# Revit family: UNB_Specchio_Multiproduct_BIM_IT_T3588;T3589;T3590;T3591;T3592;T3593_NEW
name_source: partatom
category: Plumbing Fixtures
revit_build: Autodesk Revit 2017 (Build: 20160225_1515(x64)
units: mm (PartAtom-declared; Revit-internal decimal feet)

## family parameters
Cut with Voids When Loaded = No
Host = Face
Part Type = Normal
Room Calculation Point = No
Round Connector Dimension = Use Diameter
Shared = No

## types (6) — shared parameters
Accessori = http://www.idealstandard.it
AltezzaNominale = 700 mm  [stored 2.29659 ft]
Autore = Ideal Standard
Brand = Ideal Standard
CodiceDiPrestazione = EN
Colore = specchio
Connessione = piombatura
Default Elevation = 1500 mm
DescrizioneClassifcazioneUni2015 = Bathroom furniture
Finitura = specchio
Forma = rettangolare
Garanzia = garanzia del produttore
IfcEsportaCome = BATHROOM FURNITURE
InformazioniDiProdotto = http://www.idealstandard.it
InstruzioniInstallazione = http://www.idealstandard.it
LunghezzaNominale = 170 mm
Materiale = bicchiere
PartiDiRicambio = http://www.idealstandard.it
ProfonditàNominale = 170 mm
Revisione = 1
RiferimentoClassificazioneUni2015 = MIRRORS
Spazio = interno
Telefono = 800 652 290
TipoDiDato = Fisso
TipoEspotazioneIfc = IfcFurnitureType
TipologiaVaso = Altro
URL = http://www.idealstandard.it
UnitàDurata = anno
UnitàDurataGaranzia = anno
UnitàLineare = millimetro
UnitàMonetaria = €
UnitàSuperficie = millimetro
UnitàVolume = litro
Versione = 1
VersioneClassificazioneUni2015 = IfcFurnitureType
zero-valued in all types: Cost, CostoDiSostituzione

## per-type parameters (varying)
| type | Caratteristiche | CodiceABarre | Description | DoubleUnitsOnly | LarghezzaNominale | Model | ModelloDiRiferimento | Nome | NomeOggettoBim | NumeroDiModello | PesoNetto | Riferimento | SingleUnitsOnly |
| T3588 - 500 x 700 mirror cabinets | SPECCHIO CONT. LOW 50X70 MATT AL | 8014140447870 | SPECCHIO CONT. LOW 50X70 MATT AL | No | 500 mm | T3588AL | SPECCHIO CONT. LOW 50X70 MATT AL | ISI_IdealStandard_Specchio_T3588 | ISI_IdealStandard_Specchio_T3588 | T3588AL | 14.50 Kg | T3588 | Yes |
| T3589 - 600 x 700 mirror cabinets | SPECCHIO CONT. LOW 60X70 MATT AL | 8014140447894 | SPECCHIO CONT. LOW 60X70 MATT AL | No | 600 mm | T3589AL | SPECCHIO CONT. LOW 60X70 MATT AL | ISI_IdealStandard_Specchio_T3589 | ISI_IdealStandard_Specchio_T3589 | T3589AL | 16.00 Kg | T3589 | Yes |
| T3590 - 700 x 700 mirror cabinets | SPECCHIO CONT. LOW 70X70 MATT AL | 8014140447917 | SPECCHIO CONT. LOW 70X70 MATT AL | Yes | 700 mm  [stored 2.29659 ft] | T3590AL | SPECCHIO CONT. LOW 70X70 MATT AL | ISI_IdealStandard_Specchio_T3590 | ISI_IdealStandard_Specchio_T3590 | T3590AL | 18.00 Kg | T3590 | No |
| T3591 - 800 x 700 mirror cabinets | SPECCHIO CONT. LOW 80X70 MATT AL | 8014140447931 | SPECCHIO CONT. LOW 80X70 MATT AL | Yes | 800 mm | T3591AL | SPECCHIO CONT. LOW 80X70 MATT AL | ISI_IdealStandard_Specchio_T3591 | ISI_IdealStandard_Specchio_T3591 | T3591AL | 20.00 Kg | T3591 | No |
| T3592 - 1000 x 700 mirror cabinets | SPECCHIO CONT. LOW 100X70 MATT AL | 8014140447955 | SPECCHIO CONT. LOW 100X70 MATT AL | Yes | 1000 mm | T3592AL | SPECCHIO CONT. LOW 100X70 MATT AL | ISI_IdealStandard_Specchio_T3592 | ISI_IdealStandard_Specchio_T3592 | T3592AL | 24.00 Kg | T3592 | No |
| T3593 - 1200 x 700 mirror cabinets | SPECCHIO CONT. LOW 120X70 MATT AL | 8014140447979 | SPECCHIO CONT. LOW 120X70 MATT AL | Yes | 1200 mm  [stored 3.93701 ft] | T3593AL | SPECCHIO CONT. LOW 120X70 MATT AL | ISI_IdealStandard_Specchio_T3593 | ISI_IdealStandard_Specchio_T3593 | T3593AL | 26.00 Kg | T3593 | No |

note: [stored X ft] marks values corroborated as IEEE doubles in the binary element streams (Revit-internal decimal feet)

## geometry (parser evidence)
native form markers: Sweep x2
no freeform markers — native parametric forms only
